AUTODESK INVENTOR PART (.ipt)
format: ipt  version: 2021 (Build 250183000, 183)  size: 97,792 bytes
history: native  units: in
note: dims shown in document units (in); Inventor stores cm internally (conversion verified against a paired STEP export)
features: other x2, sketch x1, reference x1
ambient origin geometry x8: Origin, YZ Plane, XZ Plane, XY Plane, X Axis, Y Axis, Z Axis, Center Point
feature tree (4):
  sketch  "Boceto1"  dims[d0=5.9055in d1=5.9055in d7=8.0498in d8=15.0448in]
  reference  "Referencia1"
  other  "nsmb_normal.iam"
  other  "eslabon_1:1"
